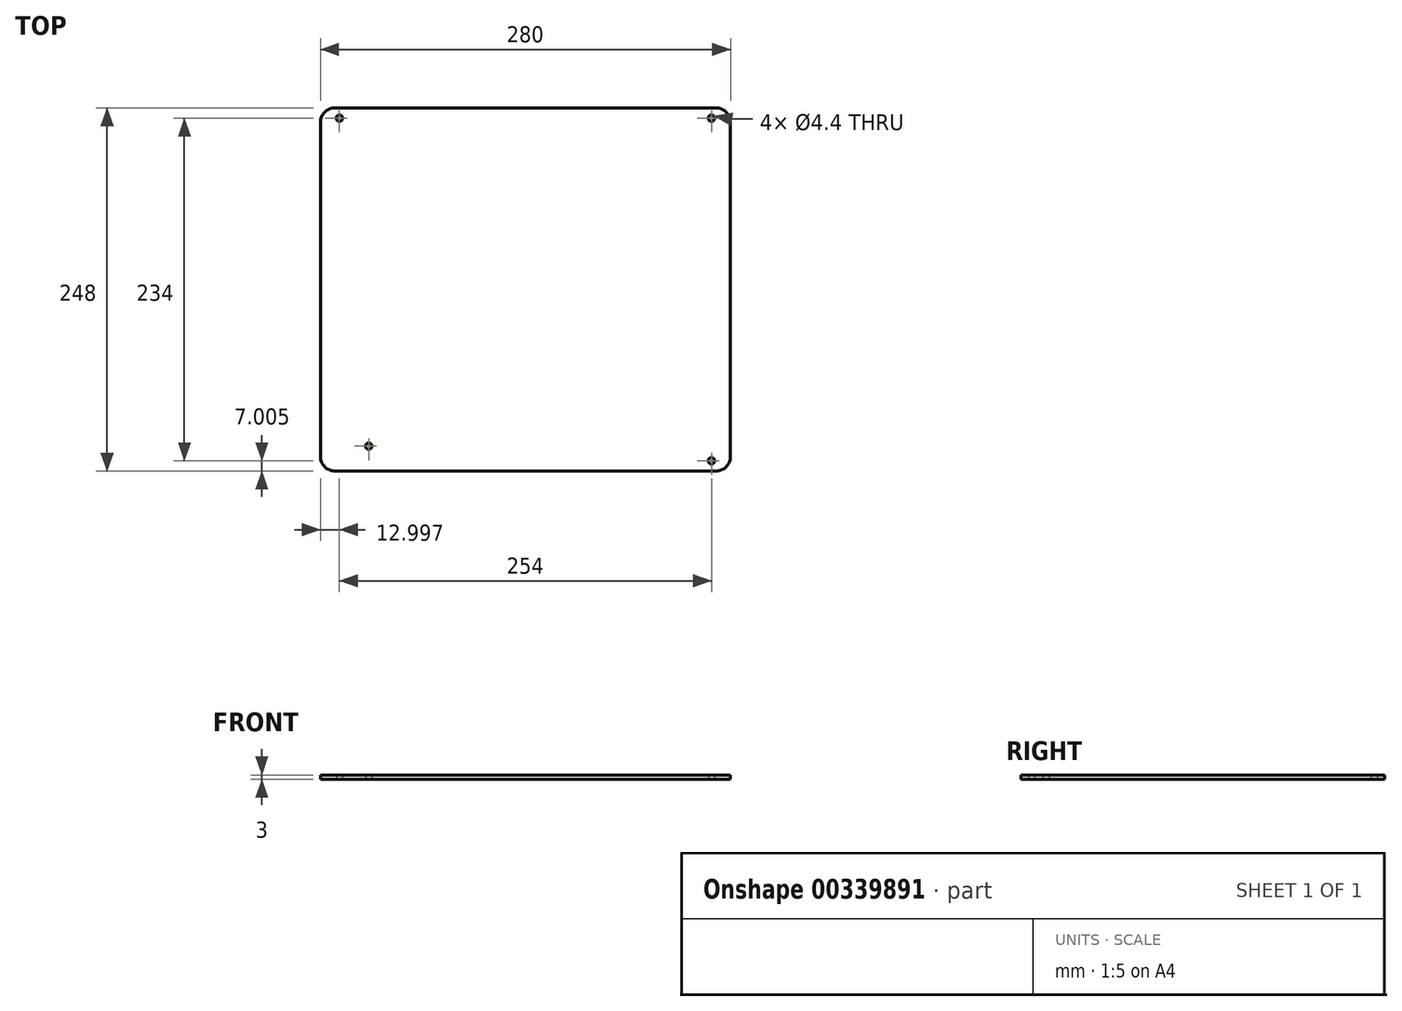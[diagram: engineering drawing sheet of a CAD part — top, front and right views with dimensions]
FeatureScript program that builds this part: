
annotation { "Feature Type Name" : "Feature", "Feature Type Description" : "" }
export const myFeature = defineFeature(function(context is Context, id is Id, definition is map)
    precondition{}
    {
        {
            var Q0;
            Q0=qCreatedBy(makeId("Top.planeOp"),FACE);
            var sketch = newSketch(context, id + "F0", { "sketchPlane" : qUnion([Q0])});
            skLineSegment(sketch, "E0.bottom", {"start": v(-160.67, 55.38) * mm, "end": v(119.33, 55.38) * mm});
            skLineSegment(sketch, "E0.top", {"start": v(-160.67, -192.62) * mm, "end": v(119.33, -192.62) * mm});
            skLineSegment(sketch, "E0.left", {"start": v(-160.67, 55.38) * mm, "end": v(-160.67, -192.62) * mm});
            skLineSegment(sketch, "E0.right", {"start": v(119.33, 55.38) * mm, "end": v(119.33, -192.62) * mm});
            skLineSegment(sketch, "E1.bottom", {"start": v(-127.67, 38.38) * mm, "end": v(86.33, 38.38) * mm, "construction": true});
            skLineSegment(sketch, "E1.top", {"start": v(-127.67, -175.62) * mm, "end": v(86.33, -175.62) * mm, "construction": true});
            skLineSegment(sketch, "E1.left", {"start": v(-127.67, 38.38) * mm, "end": v(-127.67, -175.62) * mm, "construction": true});
            skLineSegment(sketch, "E1.right", {"start": v(86.33, 38.38) * mm, "end": v(86.33, -175.62) * mm, "construction": true});
            skCircle(sketch, "E2", {"center": v(-147.67, 48.38) * mm, "radius": 2.2 * mm});
            skCircle(sketch, "E3", {"center": v(-127.67, -175.62) * mm, "radius": 2.2 * mm});
            skCircle(sketch, "E4", {"center": v(106.33, -185.62) * mm, "radius": 2.2 * mm});
            skCircle(sketch, "E5", {"center": v(106.33, 48.38) * mm, "radius": 2.2 * mm});
            skLineSegment(sketch, "E6.bottom", {"start": v(-147.67, 48.38) * mm, "end": v(106.33, 48.38) * mm, "construction": true});
            skLineSegment(sketch, "E6.top", {"start": v(-147.67, -185.62) * mm, "end": v(106.33, -185.62) * mm, "construction": true});
            skLineSegment(sketch, "E6.left", {"start": v(-147.67, 48.38) * mm, "end": v(-147.67, -185.62) * mm, "construction": true});
            skLineSegment(sketch, "E6.right", {"start": v(106.33, 48.38) * mm, "end": v(106.33, -185.62) * mm, "construction": true});
            skSolve(sketch);
        }
        {
            var Q0;
            Q0=makeQuery(id+"F0.imprint","IMPRINT",FACE,{"disambiguationData":[TD([[makeQuery(id+"F0.imprint","IMPRINT",EDGE,{"derivedFrom":sQuery(id+"F0.wireOp",EDGE,"E0.bottom")}),-1.0]])]});
            extrude(context, id + "F1", {"entities" : qUnion([Q0]), "depth" : 3 * mm, "offsetDistance" : 25 * mm});
        }
        {
            var Q0;
            Q0=makeQuery(id+"F1.opExtrude","SWEPT_EDGE",EDGE,{"disambiguationData":[OSD([sQuery(id+"F0.wireOp",EDGE,"E0.bottom"),sQuery(id+"F0.wireOp",EDGE,"E0.left")])]});
            var Q1;
            Q1=makeQuery(id+"F1.opExtrude","SWEPT_EDGE",EDGE,{"disambiguationData":[OSD([sQuery(id+"F0.wireOp",EDGE,"E0.bottom"),sQuery(id+"F0.wireOp",EDGE,"E0.right")])]});
            var Q2;
            Q2=makeQuery(id+"F1.opExtrude","SWEPT_EDGE",EDGE,{"disambiguationData":[OSD([sQuery(id+"F0.wireOp",EDGE,"E0.top"),sQuery(id+"F0.wireOp",EDGE,"E0.right")])]});
            var Q3;
            Q3=makeQuery(id+"F1.opExtrude","SWEPT_EDGE",EDGE,{"disambiguationData":[OSD([sQuery(id+"F0.wireOp",EDGE,"E0.top"),sQuery(id+"F0.wireOp",EDGE,"E0.left")])]});
            fillet(context, id + "F2", {"entities" : qUnion([Q0, Q1, Q2, Q3]), "radius" : 10 * mm, "tangentPropagation" : true, "allowEdgeOverflow" : false});
        }
    });
